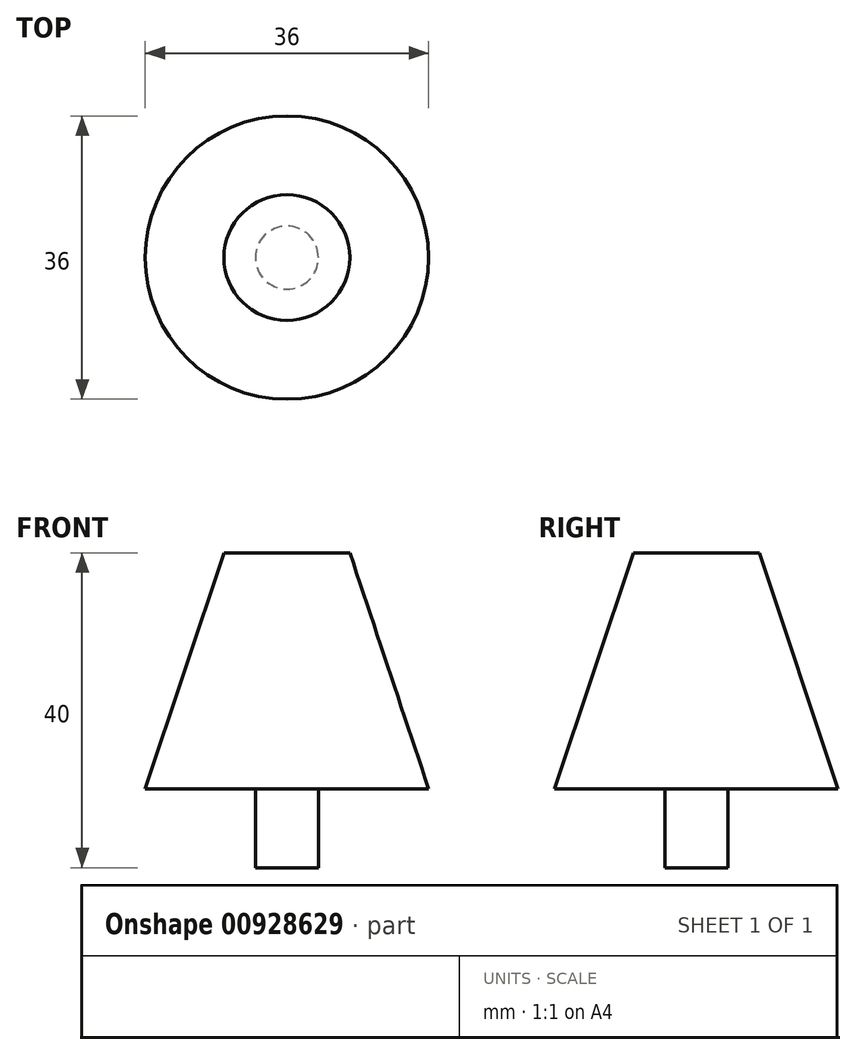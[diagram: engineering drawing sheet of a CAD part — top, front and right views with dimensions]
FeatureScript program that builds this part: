
annotation { "Feature Type Name" : "Feature", "Feature Type Description" : "" }
export const myFeature = defineFeature(function(context is Context, id is Id, definition is map)
    precondition{}
    {
        {
            var Q0;
            Q0=qCreatedBy(makeId("Front.planeOp"),FACE);
            var sketch = newSketch(context, id + "F0", { "sketchPlane" : qUnion([Q0])});
            skLineSegment(sketch, "E0", {"start": v(0, 40) * mm, "end": v(-8, 40) * mm});
            skLineSegment(sketch, "E1", {"start": v(-8, 40) * mm, "end": v(-18, 10) * mm});
            skLineSegment(sketch, "E2", {"start": v(-18, 10) * mm, "end": v(-4, 10) * mm});
            skLineSegment(sketch, "E3", {"start": v(-4, 10) * mm, "end": v(-4, 0) * mm});
            skLineSegment(sketch, "E4", {"start": v(-4, 0) * mm, "end": v(0, 0) * mm});
            skLineSegment(sketch, "E5", {"start": v(0, 40) * mm, "end": v(0, 0) * mm});
            skLineSegment(sketch, "E6", {"start": v(0, 57.71) * mm, "end": v(0, -16.02) * mm, "construction": true});
            skSolve(sketch);
        }
        {
            var Q0;
            Q0 = qSketchRegion(id + "F0", true);
            var Q1;
            Q1=sQuery(id+"F0.wireOp",EDGE,"E6");
            revolve(context, id + "F1", {"surfaceOperationType" : NewSurfaceOperationType.NEW, "entities" : qUnion([Q0]), "axis" : qUnion([Q1]), "revolveType" : RevolveType.FULL});
        }
    });
